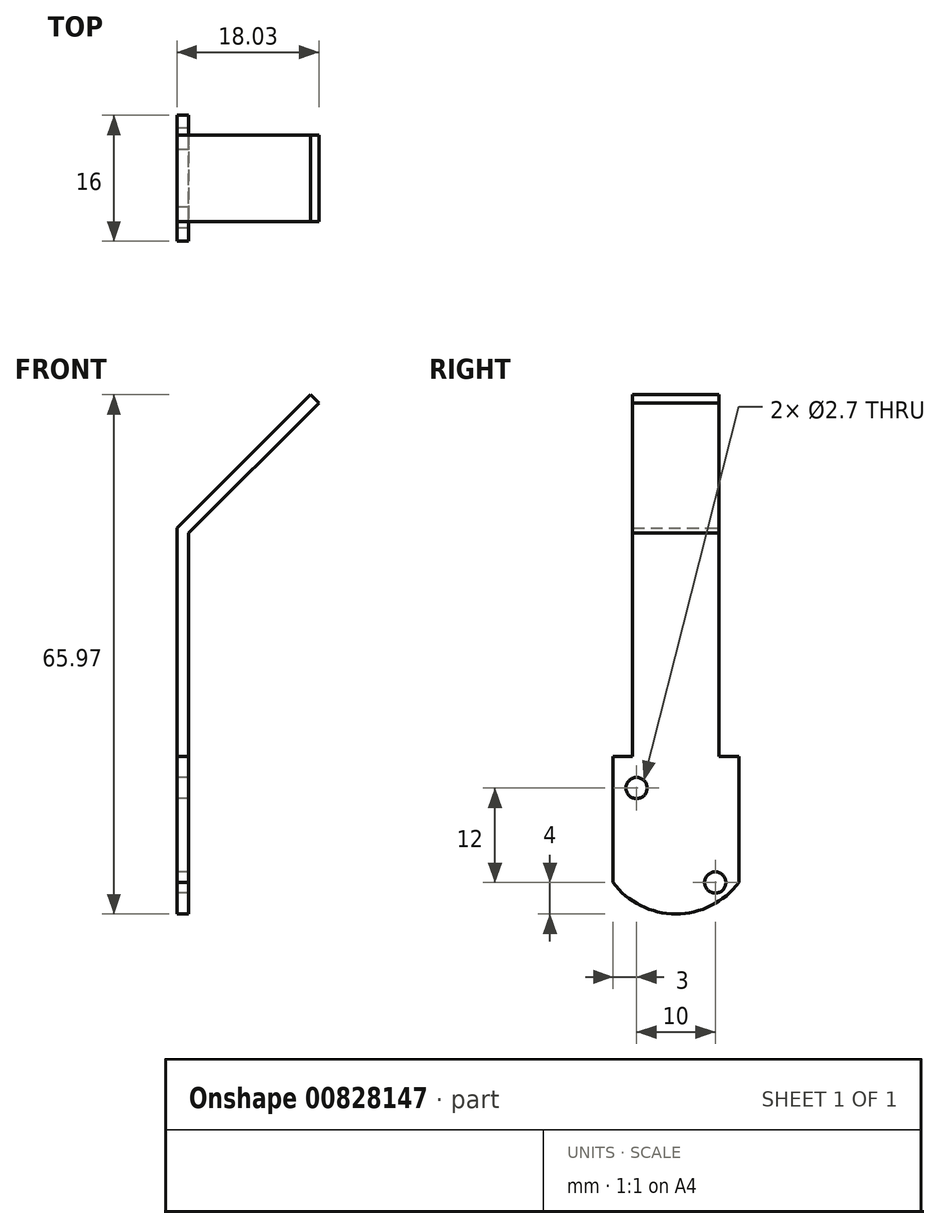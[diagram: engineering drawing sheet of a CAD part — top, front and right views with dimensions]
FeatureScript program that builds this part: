
annotation { "Feature Type Name" : "Feature", "Feature Type Description" : "" }
export const myFeature = defineFeature(function(context is Context, id is Id, definition is map)
    precondition{}
    {
        {
            var Q0;
            Q0=qCreatedBy(makeId("Front.planeOp"),FACE);
            var sketch = newSketch(context, id + "F0", { "sketchPlane" : qUnion([Q0])});
            skLineSegment(sketch, "E0.bottom", {"start": v(0, 0) * mm, "end": v(1.5, 0) * mm});
            skLineSegment(sketch, "E0.left", {"start": v(0, 0) * mm, "end": v(0, 49) * mm});
            skLineSegment(sketch, "E0.right", {"start": v(1.5, 0) * mm, "end": v(1.5, 48.38) * mm});
            skLineSegment(sketch, "E1", {"start": v(0, 49) * mm, "end": v(16.97, 65.97) * mm});
            skLineSegment(sketch, "E2", {"start": v(16.97, 65.97) * mm, "end": v(18.03, 64.9) * mm});
            skLineSegment(sketch, "E3", {"start": v(18.03, 64.9) * mm, "end": v(1.5, 48.38) * mm});
            skSolve(sketch);
        }
        {
            var Q0;
            Q0=qSketchRegion(id+"F0",true);
            extrude(context, id + "F1", {"entities" : qUnion([Q0]), "depth" : 16 * mm, "offsetDistance" : 25 * mm});
        }
        {
            var Q0;
            Q0=qCreatedBy(makeId("Right.planeOp"),FACE);
            var sketch = newSketch(context, id + "F2", { "sketchPlane" : qUnion([Q0])});
            skLineSegment(sketch, "E4.bottom", {"start": v(6.57, 65.97) * mm, "end": v(-2.5, 65.97) * mm});
            skLineSegment(sketch, "E4.top", {"start": v(6.57, 20) * mm, "end": v(-2.5, 20) * mm});
            skLineSegment(sketch, "E4.left", {"start": v(6.57, 65.97) * mm, "end": v(6.57, 20) * mm});
            skLineSegment(sketch, "E4.right", {"start": v(-2.5, 65.97) * mm, "end": v(-2.5, 20) * mm});
            skLineSegment(sketch, "E5.bottom", {"start": v(-23.43, 65.97) * mm, "end": v(-13.5, 65.97) * mm});
            skLineSegment(sketch, "E5.top", {"start": v(-23.43, 20) * mm, "end": v(-13.5, 20) * mm});
            skLineSegment(sketch, "E5.left", {"start": v(-23.43, 65.97) * mm, "end": v(-23.43, 20) * mm});
            skLineSegment(sketch, "E5.right", {"start": v(-13.5, 65.97) * mm, "end": v(-13.5, 20) * mm});
            skSolve(sketch);
        }
        {
            var Q0;
            Q0=qSketchRegion(id+"F2",true);
            extrude(context, id + "F3", {"entities" : qUnion([Q0]), "operationType" : NewBodyOperationType.REMOVE, "depth" : 25 * mm, "offsetDistance" : 25 * mm});
        }
        {
            var Q0;
            Q0=makeQuery(id+"F1.opExtrude","SWEPT_FACE",FACE,{"disambiguationData":[OSD([sQuery(id+"F0.wireOp",EDGE,"E0.left")])]});
            var sketch = newSketch(context, id + "F4", { "sketchPlane" : qUnion([Q0])});
            skArc(sketch, "E6", {"start": v(-2, 10) * mm, "mid": v(8, 0) * mm, "end": v(18, 10) * mm});
            skLineSegment(sketch, "E7", {"start": v(8, 49) * mm, "end": v(8, 0) * mm, "construction": true});
            skLineSegment(sketch, "E8", {"start": v(-2, 10) * mm, "end": v(-2, -2.5) * mm});
            skLineSegment(sketch, "E9", {"start": v(-2, -2.5) * mm, "end": v(18, -2.5) * mm});
            skLineSegment(sketch, "E10", {"start": v(18, -2.5) * mm, "end": v(18, 10) * mm});
            skSolve(sketch);
        }
        {
            var Q0;
            Q0=qSketchRegion(id+"F4",true);
            extrude(context, id + "F5", {"entities" : qUnion([Q0]), "operationType" : NewBodyOperationType.REMOVE, "endBound" : BoundingType.THROUGH_ALL, "oppositeDirection" : true, "depth" : 25 * mm, "offsetDistance" : 25 * mm});
        }
        {
            var Q0;
            Q0=makeQuery(id+"F1.opExtrude","SWEPT_FACE",FACE,{"disambiguationData":[OSD([sQuery(id+"F0.wireOp",EDGE,"E0.left")])]});
            var sketch = newSketch(context, id + "F6", { "sketchPlane" : qUnion([Q0])});
            skCircle(sketch, "E11", {"center": v(3, 16) * mm, "radius": 1.35 * mm, "construction": true});
            skCircle(sketch, "E12", {"center": v(13, 4) * mm, "radius": 1.35 * mm, "construction": true});
            skLineSegment(sketch, "E13.bottom", {"start": v(3, 16) * mm, "end": v(13, 16) * mm, "construction": true});
            skLineSegment(sketch, "E13.top", {"start": v(3, 4) * mm, "end": v(13, 4) * mm, "construction": true});
            skLineSegment(sketch, "E13.left", {"start": v(3, 16) * mm, "end": v(3, 4) * mm, "construction": true});
            skLineSegment(sketch, "E13.right", {"start": v(13, 16) * mm, "end": v(13, 4) * mm, "construction": true});
            skCircle(sketch, "E14", {"center": v(13, 16) * mm, "radius": 1.35 * mm});
            skCircle(sketch, "E15", {"center": v(3, 4) * mm, "radius": 1.35 * mm});
            skSolve(sketch);
        }
        {
            var Q0;
            Q0=qSketchRegion(id+"F6",true);
            extrude(context, id + "F7", {"entities" : qUnion([Q0]), "operationType" : NewBodyOperationType.REMOVE, "endBound" : BoundingType.THROUGH_ALL, "oppositeDirection" : true, "depth" : 25 * mm, "offsetDistance" : 25 * mm});
        }
        {
            var Q0;
            Q0 = qSketchRegion(id + "F6", true);
            extrude(context, id + "F8", {"entities" : qUnion([Q0]), "operationType" : NewBodyOperationType.REMOVE, "endBound" : BoundingType.THROUGH_ALL, "oppositeDirection" : true, "depth" : 25 * mm, "offsetDistance" : 25 * mm});
        }
    });
